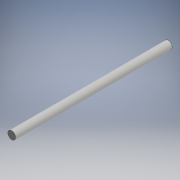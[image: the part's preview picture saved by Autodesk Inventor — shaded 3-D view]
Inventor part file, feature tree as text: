
AUTODESK INVENTOR PART (.ipt)
format: ipt  version: 2018 (Build 220112000, 112)  size: 116,736 bytes
history: native  units: mm
features: other x1, sketch x1
ambient origin geometry x8: Origin, YZ Plane, XZ Plane, XY Plane, X Axis, Y Axis, Z Axis, Center Point
bodies: Volumenkörper1 (feature_tree)
feature tree (2):
  other  "reifen_achse"
  sketch  "Skizze1"  dims[d0=8.0mm d1=160.0mm d2=0.0mm]
